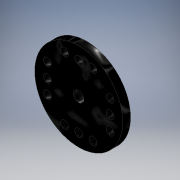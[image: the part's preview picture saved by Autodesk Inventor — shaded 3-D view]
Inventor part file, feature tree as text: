
AUTODESK INVENTOR PART (.ipt)
format: ipt  version: 2018 (Build 220112000, 112)  size: 148,480 bytes
history: native  units: mm
features: extrude x4, sketch x4, pattern_circular x1
ambient origin geometry x8: Origin, YZ Plane, XZ Plane, XY Plane, X Axis, Y Axis, Z Axis, Center Point
bodies: Solid1 (feature_tree)
feature tree (9):
  extrude  "Extrusion1"  Depth=1.9mm TaperAngle=0.0deg
  extrude  "Extrusion2"  Depth=3.5mm TaperAngle=0.0deg
  extrude  "Extrusion3"  Depth=3.5mm TaperAngle=0.0deg
  extrude  "Extrusion4"  Depth=7.5mm
  pattern_circular  "Circular Pattern1"  [2 undecoded]
  sketch  "Sketch1"  dims[d0=21.0mm d1=1.9mm d2=0.0mm]
  sketch  "Sketch2"  dims[d3=8.8mm d4=3.5mm d5=0.0mm]
  sketch  "Sketch3"  dims[d6=2.5mm d7=3.5mm d8=0.0mm]
  sketch  "Sketch4"  dims[d9=1.9mm d10=7.5mm d11=1.9mm d12=3.4mm d13=7.5mm d14=1.9mm d15=3.4mm d16=7.5mm d17=3.5mm d18=0.0mm d19=40.0mm d20=360.0deg]
note: 2 required parameter values undecoded (feature->parameter linkage not recoverable at this tier; creation-order binding heuristic only, values carry confidence <= 0.55)
